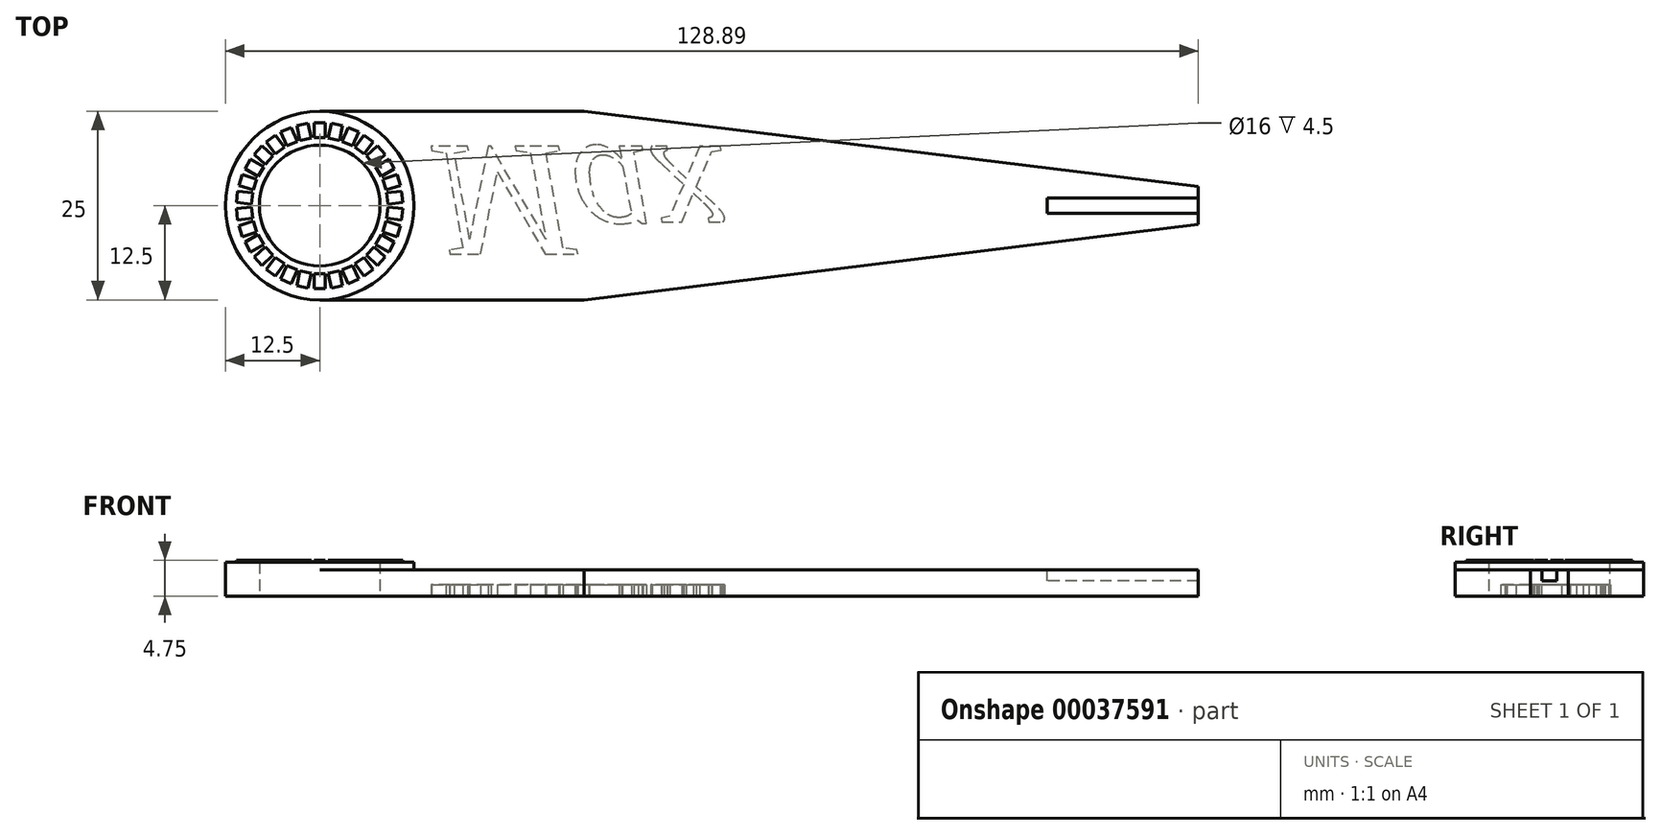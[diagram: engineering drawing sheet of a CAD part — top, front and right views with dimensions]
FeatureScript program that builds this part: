
annotation { "Feature Type Name" : "Feature", "Feature Type Description" : "" }
export const myFeature = defineFeature(function(context is Context, id is Id, definition is map)
    precondition{}
    {
        {
            var Q0;
            Q0=qCreatedBy(makeId("Top.planeOp"),FACE);
            var sketch = newSketch(context, id + "F0", { "sketchPlane" : qUnion([Q0])});
            skArc(sketch, "E0", {"start": v(0, 12.5) * mm, "mid": v(-12.5, 0) * mm, "end": v(0, -12.5) * mm});
            skLineSegment(sketch, "E1", {"start": v(0, 12.5) * mm, "end": v(35, 12.5) * mm});
            skPoint(sketch, "E2", {"position": v(0, 12.5) * mm});
            skPoint(sketch, "E3", {"position": v(0, -12.5) * mm});
            skLineSegment(sketch, "E4", {"start": v(35, 12.5) * mm, "end": v(90.9, 12.5) * mm, "construction": true});
            skLineSegment(sketch, "E5", {"start": v(35, 12.5) * mm, "end": v(116.39, 2.5) * mm});
            skLineSegment(sketch, "E6", {"start": v(0, 0) * mm, "end": v(34.77, 0) * mm, "construction": true});
            skLineSegment(sketch, "E7.MirrorCS", {"start": v(0, -12.5) * mm, "end": v(35, -12.5) * mm});
            skLineSegment(sketch, "E8.MirrorCS", {"start": v(35, -12.5) * mm, "end": v(116.39, -2.5) * mm});
            skCircle(sketch, "E9", {"center": v(0, 0) * mm, "radius": 8 * mm});
            skLineSegment(sketch, "E10", {"start": v(116.39, 2.5) * mm, "end": v(116.39, -2.5) * mm});
            skSolve(sketch);
        }
        {
            var Q0;
            Q0 = qSketchRegion(id + "F0", true);
            extrude(context, id + "F1", {"entities" : qUnion([Q0]), "depth" : 3.5 * mm});
        }
        {
            var Q0;
            Q0=makeQuery(id+"F1.opExtrude","CAP_FACE",FACE,{"disambiguationData":[OSD([sQuery(id+"F0.wireOp",EDGE,"E0"),sQuery(id+"F0.wireOp",EDGE,"E1"),sQuery(id+"F0.wireOp",EDGE,"E5"),sQuery(id+"F0.wireOp",EDGE,"E7.MirrorCS"),sQuery(id+"F0.wireOp",EDGE,"E8.MirrorCS"),sQuery(id+"F0.wireOp",EDGE,"E9"),sQuery(id+"F0.wireOp",EDGE,"E10")])],"isStart":false});
            var sketch = newSketch(context, id + "F2", { "sketchPlane" : qUnion([Q0])});
            skCircle(sketch, "E11", {"center": v(0, 0) * mm, "radius": 8 * mm});
            skCircle(sketch, "E12", {"center": v(0, 0) * mm, "radius": 12.5 * mm});
            skSolve(sketch);
        }
        {
            var Q0;
            Q0 = qSketchRegion(id + "F2", true);
            extrude(context, id + "F3", {"entities" : qUnion([Q0]), "operationType" : NewBodyOperationType.ADD, "depth" : 1 * mm});
        }
        {
            var Q0;
            Q0=makeQuery(id+"F3.opExtrude","CAP_FACE",FACE,{"disambiguationData":[OSD([sQuery(id+"F2.wireOp",EDGE,"E11"),sQuery(id+"F2.wireOp",EDGE,"E12")])],"isStart":false});
            var sketch = newSketch(context, id + "F4", { "sketchPlane" : qUnion([Q0])});
            skLineSegment(sketch, "E13.bottom", {"start": v(-0.75, 11) * mm, "end": v(0.75, 11) * mm});
            skLineSegment(sketch, "E13.top", {"start": v(-0.75, 9) * mm, "end": v(0.75, 9) * mm});
            skLineSegment(sketch, "E13.left", {"start": v(-0.75, 11) * mm, "end": v(-0.75, 9) * mm});
            skLineSegment(sketch, "E13.right", {"start": v(0.75, 11) * mm, "end": v(0.75, 9) * mm});
            skLineSegment(sketch, "E14.1.0", {"start": v(-3.02, 10.6) * mm, "end": v(-1.55, 10.92) * mm});
            skLineSegment(sketch, "E14.1.1", {"start": v(-2.6, 8.65) * mm, "end": v(-1.14, 8.96) * mm});
            skLineSegment(sketch, "E14.1.2", {"start": v(-1.55, 10.92) * mm, "end": v(-1.14, 8.96) * mm});
            skLineSegment(sketch, "E14.1.3", {"start": v(-3.02, 10.6) * mm, "end": v(-2.6, 8.65) * mm});
            skLineSegment(sketch, "E14.2.0", {"start": v(-5.16, 9.74) * mm, "end": v(-3.79, 10.35) * mm});
            skLineSegment(sketch, "E14.2.1", {"start": v(-4.35, 7.92) * mm, "end": v(-2.98, 8.53) * mm});
            skLineSegment(sketch, "E14.2.2", {"start": v(-3.79, 10.35) * mm, "end": v(-2.98, 8.53) * mm});
            skLineSegment(sketch, "E14.2.3", {"start": v(-5.16, 9.74) * mm, "end": v(-4.35, 7.92) * mm});
            skLineSegment(sketch, "E14.3.0", {"start": v(-7.07, 8.46) * mm, "end": v(-5.86, 9.34) * mm});
            skLineSegment(sketch, "E14.3.1", {"start": v(-5.9, 6.84) * mm, "end": v(-4.68, 7.72) * mm});
            skLineSegment(sketch, "E14.3.2", {"start": v(-5.86, 9.34) * mm, "end": v(-4.68, 7.72) * mm});
            skLineSegment(sketch, "E14.3.3", {"start": v(-7.07, 8.46) * mm, "end": v(-5.9, 6.84) * mm});
            skLineSegment(sketch, "E14.4.0", {"start": v(-8.68, 6.8) * mm, "end": v(-7.67, 7.92) * mm});
            skLineSegment(sketch, "E14.4.1", {"start": v(-7.2, 5.46) * mm, "end": v(-6.19, 6.58) * mm});
            skLineSegment(sketch, "E14.4.2", {"start": v(-7.67, 7.92) * mm, "end": v(-6.19, 6.58) * mm});
            skLineSegment(sketch, "E14.4.3", {"start": v(-8.68, 6.8) * mm, "end": v(-7.2, 5.46) * mm});
            skLineSegment(sketch, "E14.5.0", {"start": v(-9.9, 4.85) * mm, "end": v(-9.15, 6.15) * mm});
            skLineSegment(sketch, "E14.5.1", {"start": v(-8.17, 3.85) * mm, "end": v(-7.42, 5.15) * mm});
            skLineSegment(sketch, "E14.5.2", {"start": v(-9.15, 6.15) * mm, "end": v(-7.42, 5.15) * mm});
            skLineSegment(sketch, "E14.5.3", {"start": v(-9.9, 4.85) * mm, "end": v(-8.17, 3.85) * mm});
            skLineSegment(sketch, "E14.6.0", {"start": v(-10.7, 2.69) * mm, "end": v(-10.23, 4.11) * mm});
            skLineSegment(sketch, "E14.6.1", {"start": v(-8.8, 2.07) * mm, "end": v(-8.33, 3.5) * mm});
            skLineSegment(sketch, "E14.6.2", {"start": v(-10.23, 4.11) * mm, "end": v(-8.33, 3.5) * mm});
            skLineSegment(sketch, "E14.6.3", {"start": v(-10.7, 2.69) * mm, "end": v(-8.8, 2.07) * mm});
            skLineSegment(sketch, "E14.7.0", {"start": v(-11.02, 0.4) * mm, "end": v(-10.86, 1.9) * mm});
            skLineSegment(sketch, "E14.7.1", {"start": v(-9.03, 0.2) * mm, "end": v(-8.87, 1.69) * mm});
            skLineSegment(sketch, "E14.7.2", {"start": v(-10.86, 1.9) * mm, "end": v(-8.87, 1.69) * mm});
            skLineSegment(sketch, "E14.7.3", {"start": v(-11.02, 0.4) * mm, "end": v(-9.03, 0.2) * mm});
            skLineSegment(sketch, "E14.8.0", {"start": v(-10.86, -1.9) * mm, "end": v(-11.02, -0.4) * mm});
            skLineSegment(sketch, "E14.8.1", {"start": v(-8.87, -1.69) * mm, "end": v(-9.03, -0.2) * mm});
            skLineSegment(sketch, "E14.8.2", {"start": v(-11.02, -0.4) * mm, "end": v(-9.03, -0.2) * mm});
            skLineSegment(sketch, "E14.8.3", {"start": v(-10.86, -1.9) * mm, "end": v(-8.87, -1.69) * mm});
            skLineSegment(sketch, "E14.9.0", {"start": v(-10.23, -4.11) * mm, "end": v(-10.7, -2.69) * mm});
            skLineSegment(sketch, "E14.9.1", {"start": v(-8.33, -3.5) * mm, "end": v(-8.8, -2.07) * mm});
            skLineSegment(sketch, "E14.9.2", {"start": v(-10.7, -2.69) * mm, "end": v(-8.8, -2.07) * mm});
            skLineSegment(sketch, "E14.9.3", {"start": v(-10.23, -4.11) * mm, "end": v(-8.33, -3.5) * mm});
            skLineSegment(sketch, "E14.10.0", {"start": v(-9.15, -6.15) * mm, "end": v(-9.9, -4.85) * mm});
            skLineSegment(sketch, "E14.10.1", {"start": v(-7.42, -5.15) * mm, "end": v(-8.17, -3.85) * mm});
            skLineSegment(sketch, "E14.10.2", {"start": v(-9.9, -4.85) * mm, "end": v(-8.17, -3.85) * mm});
            skLineSegment(sketch, "E14.10.3", {"start": v(-9.15, -6.15) * mm, "end": v(-7.42, -5.15) * mm});
            skLineSegment(sketch, "E14.11.0", {"start": v(-7.67, -7.92) * mm, "end": v(-8.68, -6.8) * mm});
            skLineSegment(sketch, "E14.11.1", {"start": v(-6.19, -6.58) * mm, "end": v(-7.2, -5.46) * mm});
            skLineSegment(sketch, "E14.11.2", {"start": v(-8.68, -6.8) * mm, "end": v(-7.2, -5.46) * mm});
            skLineSegment(sketch, "E14.11.3", {"start": v(-7.67, -7.92) * mm, "end": v(-6.19, -6.58) * mm});
            skLineSegment(sketch, "E14.12.0", {"start": v(-5.86, -9.34) * mm, "end": v(-7.07, -8.46) * mm});
            skLineSegment(sketch, "E14.12.1", {"start": v(-4.68, -7.72) * mm, "end": v(-5.9, -6.84) * mm});
            skLineSegment(sketch, "E14.12.2", {"start": v(-7.07, -8.46) * mm, "end": v(-5.9, -6.84) * mm});
            skLineSegment(sketch, "E14.12.3", {"start": v(-5.86, -9.34) * mm, "end": v(-4.68, -7.72) * mm});
            skLineSegment(sketch, "E14.13.0", {"start": v(-3.79, -10.35) * mm, "end": v(-5.16, -9.74) * mm});
            skLineSegment(sketch, "E14.13.1", {"start": v(-2.98, -8.53) * mm, "end": v(-4.35, -7.92) * mm});
            skLineSegment(sketch, "E14.13.2", {"start": v(-5.16, -9.74) * mm, "end": v(-4.35, -7.92) * mm});
            skLineSegment(sketch, "E14.13.3", {"start": v(-3.79, -10.35) * mm, "end": v(-2.98, -8.53) * mm});
            skLineSegment(sketch, "E14.14.0", {"start": v(-1.55, -10.92) * mm, "end": v(-3.02, -10.6) * mm});
            skLineSegment(sketch, "E14.14.1", {"start": v(-1.14, -8.96) * mm, "end": v(-2.6, -8.65) * mm});
            skLineSegment(sketch, "E14.14.2", {"start": v(-3.02, -10.6) * mm, "end": v(-2.6, -8.65) * mm});
            skLineSegment(sketch, "E14.14.3", {"start": v(-1.55, -10.92) * mm, "end": v(-1.14, -8.96) * mm});
            skLineSegment(sketch, "E14.15.0", {"start": v(0.75, -11) * mm, "end": v(-0.75, -11) * mm});
            skLineSegment(sketch, "E14.15.1", {"start": v(0.75, -9) * mm, "end": v(-0.75, -9) * mm});
            skLineSegment(sketch, "E14.15.2", {"start": v(-0.75, -11) * mm, "end": v(-0.75, -9) * mm});
            skLineSegment(sketch, "E14.15.3", {"start": v(0.75, -11) * mm, "end": v(0.75, -9) * mm});
            skLineSegment(sketch, "E14.16.0", {"start": v(3.02, -10.6) * mm, "end": v(1.55, -10.92) * mm});
            skLineSegment(sketch, "E14.16.1", {"start": v(2.6, -8.65) * mm, "end": v(1.14, -8.96) * mm});
            skLineSegment(sketch, "E14.16.2", {"start": v(1.55, -10.92) * mm, "end": v(1.14, -8.96) * mm});
            skLineSegment(sketch, "E14.16.3", {"start": v(3.02, -10.6) * mm, "end": v(2.6, -8.65) * mm});
            skLineSegment(sketch, "E14.17.0", {"start": v(5.16, -9.74) * mm, "end": v(3.79, -10.35) * mm});
            skLineSegment(sketch, "E14.17.1", {"start": v(4.35, -7.92) * mm, "end": v(2.98, -8.53) * mm});
            skLineSegment(sketch, "E14.17.2", {"start": v(3.79, -10.35) * mm, "end": v(2.98, -8.53) * mm});
            skLineSegment(sketch, "E14.17.3", {"start": v(5.16, -9.74) * mm, "end": v(4.35, -7.92) * mm});
            skLineSegment(sketch, "E14.18.0", {"start": v(7.07, -8.46) * mm, "end": v(5.86, -9.34) * mm});
            skLineSegment(sketch, "E14.18.1", {"start": v(5.9, -6.84) * mm, "end": v(4.68, -7.72) * mm});
            skLineSegment(sketch, "E14.18.2", {"start": v(5.86, -9.34) * mm, "end": v(4.68, -7.72) * mm});
            skLineSegment(sketch, "E14.18.3", {"start": v(7.07, -8.46) * mm, "end": v(5.9, -6.84) * mm});
            skLineSegment(sketch, "E14.19.0", {"start": v(8.68, -6.8) * mm, "end": v(7.67, -7.92) * mm});
            skLineSegment(sketch, "E14.19.1", {"start": v(7.2, -5.46) * mm, "end": v(6.19, -6.58) * mm});
            skLineSegment(sketch, "E14.19.2", {"start": v(7.67, -7.92) * mm, "end": v(6.19, -6.58) * mm});
            skLineSegment(sketch, "E14.19.3", {"start": v(8.68, -6.8) * mm, "end": v(7.2, -5.46) * mm});
            skLineSegment(sketch, "E14.20.0", {"start": v(9.9, -4.85) * mm, "end": v(9.15, -6.15) * mm});
            skLineSegment(sketch, "E14.20.1", {"start": v(8.17, -3.85) * mm, "end": v(7.42, -5.15) * mm});
            skLineSegment(sketch, "E14.20.2", {"start": v(9.15, -6.15) * mm, "end": v(7.42, -5.15) * mm});
            skLineSegment(sketch, "E14.20.3", {"start": v(9.9, -4.85) * mm, "end": v(8.17, -3.85) * mm});
            skLineSegment(sketch, "E14.21.0", {"start": v(10.7, -2.69) * mm, "end": v(10.23, -4.11) * mm});
            skLineSegment(sketch, "E14.21.1", {"start": v(8.8, -2.07) * mm, "end": v(8.33, -3.5) * mm});
            skLineSegment(sketch, "E14.21.2", {"start": v(10.23, -4.11) * mm, "end": v(8.33, -3.5) * mm});
            skLineSegment(sketch, "E14.21.3", {"start": v(10.7, -2.69) * mm, "end": v(8.8, -2.07) * mm});
            skLineSegment(sketch, "E14.22.0", {"start": v(11.02, -0.4) * mm, "end": v(10.86, -1.9) * mm});
            skLineSegment(sketch, "E14.22.1", {"start": v(9.03, -0.2) * mm, "end": v(8.87, -1.69) * mm});
            skLineSegment(sketch, "E14.22.2", {"start": v(10.86, -1.9) * mm, "end": v(8.87, -1.69) * mm});
            skLineSegment(sketch, "E14.22.3", {"start": v(11.02, -0.4) * mm, "end": v(9.03, -0.2) * mm});
            skLineSegment(sketch, "E14.23.0", {"start": v(10.86, 1.9) * mm, "end": v(11.02, 0.4) * mm});
            skLineSegment(sketch, "E14.23.1", {"start": v(8.87, 1.69) * mm, "end": v(9.03, 0.2) * mm});
            skLineSegment(sketch, "E14.23.2", {"start": v(11.02, 0.4) * mm, "end": v(9.03, 0.2) * mm});
            skLineSegment(sketch, "E14.23.3", {"start": v(10.86, 1.9) * mm, "end": v(8.87, 1.69) * mm});
            skLineSegment(sketch, "E14.24.0", {"start": v(10.23, 4.11) * mm, "end": v(10.7, 2.69) * mm});
            skLineSegment(sketch, "E14.24.1", {"start": v(8.33, 3.5) * mm, "end": v(8.8, 2.07) * mm});
            skLineSegment(sketch, "E14.24.2", {"start": v(10.7, 2.69) * mm, "end": v(8.8, 2.07) * mm});
            skLineSegment(sketch, "E14.24.3", {"start": v(10.23, 4.11) * mm, "end": v(8.33, 3.5) * mm});
            skLineSegment(sketch, "E14.25.0", {"start": v(9.15, 6.15) * mm, "end": v(9.9, 4.85) * mm});
            skLineSegment(sketch, "E14.25.1", {"start": v(7.42, 5.15) * mm, "end": v(8.17, 3.85) * mm});
            skLineSegment(sketch, "E14.25.2", {"start": v(9.9, 4.85) * mm, "end": v(8.17, 3.85) * mm});
            skLineSegment(sketch, "E14.25.3", {"start": v(9.15, 6.15) * mm, "end": v(7.42, 5.15) * mm});
            skLineSegment(sketch, "E14.26.0", {"start": v(7.67, 7.92) * mm, "end": v(8.68, 6.8) * mm});
            skLineSegment(sketch, "E14.26.1", {"start": v(6.19, 6.58) * mm, "end": v(7.2, 5.46) * mm});
            skLineSegment(sketch, "E14.26.2", {"start": v(8.68, 6.8) * mm, "end": v(7.2, 5.46) * mm});
            skLineSegment(sketch, "E14.26.3", {"start": v(7.67, 7.92) * mm, "end": v(6.19, 6.58) * mm});
            skLineSegment(sketch, "E14.27.0", {"start": v(5.86, 9.34) * mm, "end": v(7.07, 8.46) * mm});
            skLineSegment(sketch, "E14.27.1", {"start": v(4.68, 7.72) * mm, "end": v(5.9, 6.84) * mm});
            skLineSegment(sketch, "E14.27.2", {"start": v(7.07, 8.46) * mm, "end": v(5.9, 6.84) * mm});
            skLineSegment(sketch, "E14.27.3", {"start": v(5.86, 9.34) * mm, "end": v(4.68, 7.72) * mm});
            skLineSegment(sketch, "E14.28.0", {"start": v(3.79, 10.35) * mm, "end": v(5.16, 9.74) * mm});
            skLineSegment(sketch, "E14.28.1", {"start": v(2.98, 8.53) * mm, "end": v(4.35, 7.92) * mm});
            skLineSegment(sketch, "E14.28.2", {"start": v(5.16, 9.74) * mm, "end": v(4.35, 7.92) * mm});
            skLineSegment(sketch, "E14.28.3", {"start": v(3.79, 10.35) * mm, "end": v(2.98, 8.53) * mm});
            skLineSegment(sketch, "E14.29.0", {"start": v(1.55, 10.92) * mm, "end": v(3.02, 10.6) * mm});
            skLineSegment(sketch, "E14.29.1", {"start": v(1.14, 8.96) * mm, "end": v(2.6, 8.65) * mm});
            skLineSegment(sketch, "E14.29.2", {"start": v(3.02, 10.6) * mm, "end": v(2.6, 8.65) * mm});
            skLineSegment(sketch, "E14.29.3", {"start": v(1.55, 10.92) * mm, "end": v(1.14, 8.96) * mm});
            skPoint(sketch, "E14.center", {"position": v(0, 0) * mm});
            skSolve(sketch);
        }
        {
            var Q0;
            Q0 = qSketchRegion(id + "F4", true);
            extrude(context, id + "F5", {"entities" : qUnion([Q0]), "operationType" : NewBodyOperationType.ADD, "depth" : .25 * mm});
        }
        {
            var Q0;
            Q0=makeQuery(id+"F1.opExtrude","CAP_FACE",FACE,{"disambiguationData":[OSD([sQuery(id+"F0.wireOp",EDGE,"E0"),sQuery(id+"F0.wireOp",EDGE,"E1"),sQuery(id+"F0.wireOp",EDGE,"E5"),sQuery(id+"F0.wireOp",EDGE,"E7.MirrorCS"),sQuery(id+"F0.wireOp",EDGE,"E8.MirrorCS"),sQuery(id+"F0.wireOp",EDGE,"E9"),sQuery(id+"F0.wireOp",EDGE,"E10")])],"isStart":false});
            var sketch = newSketch(context, id + "F6", { "sketchPlane" : qUnion([Q0])});
            skLineSegment(sketch, "E15.bottom", {"start": v(149.9, 0) * mm, "end": v(125.34, 0) * mm});
            skLineSegment(sketch, "E15.top", {"start": v(149.9, 2) * mm, "end": v(125.34, 2) * mm});
            skLineSegment(sketch, "E15.left", {"start": v(149.9, 0) * mm, "end": v(149.9, 2) * mm});
            skLineSegment(sketch, "E15.right", {"start": v(125.34, 0) * mm, "end": v(125.34, 2) * mm});
            skLineSegment(sketch, "E16.bottom", {"start": v(116.39, 1) * mm, "end": v(96.39, 1) * mm});
            skLineSegment(sketch, "E16.top", {"start": v(116.39, -1) * mm, "end": v(96.39, -1) * mm});
            skLineSegment(sketch, "E16.left", {"start": v(116.39, 1) * mm, "end": v(116.39, -1) * mm});
            skLineSegment(sketch, "E16.right", {"start": v(96.39, 1) * mm, "end": v(96.39, -1) * mm});
            skSolve(sketch);
        }
        {
            var Q0;
            Q0 = qSketchRegion(id + "F6", true);
            extrude(context, id + "F7", {"entities" : qUnion([Q0]), "operationType" : NewBodyOperationType.REMOVE, "oppositeDirection" : true, "depth" : 1.5 * mm});
        }
        {
            var Q0;
            Q0=sQuery(id+"F0.wireOp",EDGE,"E1");
            var Q1;
            Q1=qCreatedBy(makeId("Top.planeOp"),FACE);
            cPlane(context, id + "F8", {"entities" : qUnion([Q0, Q1]), "cplaneType" : CPlaneType.LINE_ANGLE, "offset" : 150 * mm, "angle" : 0 * degree, "width" : 150 * mm, "height" : 150 * mm});
        }
        {
            var Q0;
            Q0=qCreatedBy(id+"F8.planeOp",FACE);
            var sketch = newSketch(context, id + "F9", { "sketchPlane" : qUnion([Q0])});
            skText(sketch, "E17", { "text": "Max", "fontName": "Tinos-Italic.ttf"});
            skPoint(sketch, "E18", {"position": v(15, 0) * mm});
            const initialGuessF9  = {"E17": [0.015, -0.00786, 1, 0, 0.01572]};
            skSetInitialGuess(sketch, initialGuessF9);
            skSolve(sketch);
        }
        {
            var Q0;
            Q0 = qSketchRegion(id + "F9", true);
            extrude(context, id + "F10", {"entities" : qUnion([Q0]), "operationType" : NewBodyOperationType.REMOVE, "oppositeDirection" : true, "depth" : 1.5 * mm});
        }
    });
